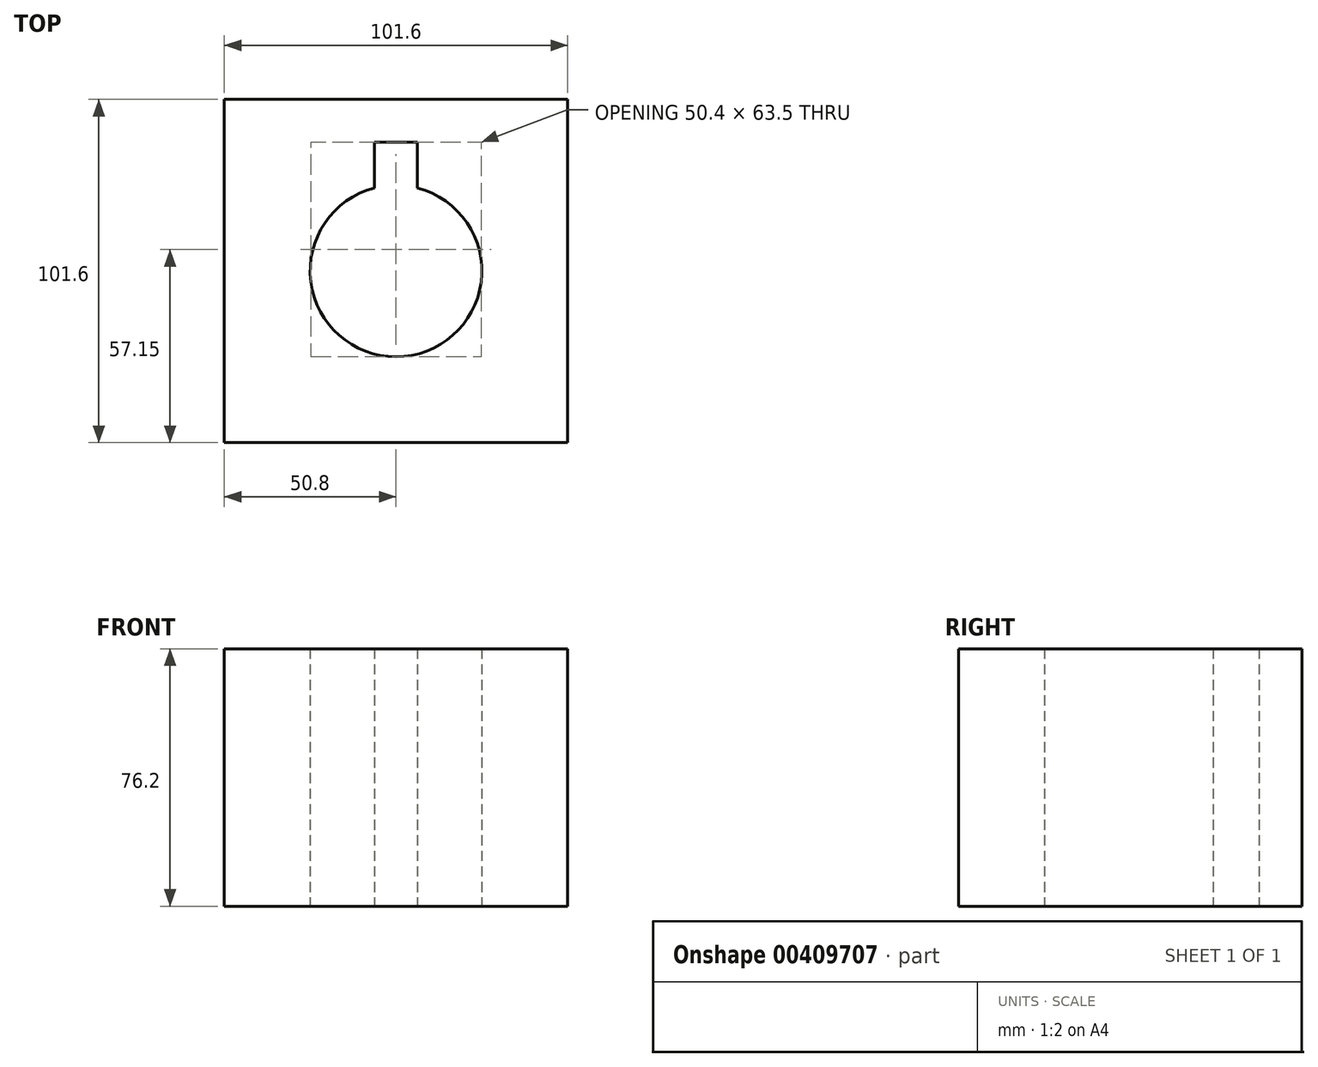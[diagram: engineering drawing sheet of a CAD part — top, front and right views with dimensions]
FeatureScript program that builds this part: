
annotation { "Feature Type Name" : "Feature", "Feature Type Description" : "" }
export const myFeature = defineFeature(function(context is Context, id is Id, definition is map)
    precondition{}
    {
        {
            var Q0;
            Q0=qCreatedBy(makeId("Top.planeOp"),FACE);
            var sketch = newSketch(context, id + "F0", { "sketchPlane" : qUnion([Q0])});
            skLineSegment(sketch, "E0", {"start": v(-6.35, 38.1) * mm, "end": v(-6.35, 24.6) * mm});
            skArc(sketch, "E1", {"start": v(-6.35, 24.6) * mm, "mid": v(0, -25.4) * mm, "end": v(6.35, 24.6) * mm});
            skLineSegment(sketch, "E2", {"start": v(-6.35, 38.1) * mm, "end": v(6.35, 38.1) * mm});
            skLineSegment(sketch, "E3", {"start": v(6.35, 38.1) * mm, "end": v(6.35, 24.6) * mm});
            skLineSegment(sketch, "E4.bottom", {"start": v(50.8, -50.8) * mm, "end": v(-50.8, -50.8) * mm});
            skLineSegment(sketch, "E4.top", {"start": v(50.8, 50.8) * mm, "end": v(-50.8, 50.8) * mm});
            skLineSegment(sketch, "E4.left", {"start": v(50.8, -50.8) * mm, "end": v(50.8, 50.8) * mm});
            skLineSegment(sketch, "E4.right", {"start": v(-50.8, -50.8) * mm, "end": v(-50.8, 50.8) * mm});
            skSolve(sketch);
        }
        {
            var Q0;
            Q0=makeQuery(id+"F0.imprint","IMPRINT",FACE,{"disambiguationData":[TD([[makeQuery(id+"F0.imprint","IMPRINT",EDGE,{"derivedFrom":sQuery(id+"F0.wireOp",EDGE,"E0")}),-1.0]])]});
            extrude(context, id + "F1", {"entities" : qUnion([Q0]), "depth" : 76.2 * mm});
        }
    });
